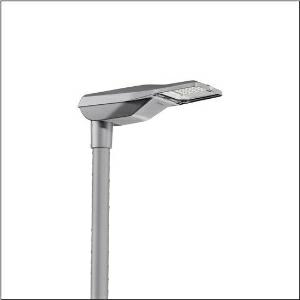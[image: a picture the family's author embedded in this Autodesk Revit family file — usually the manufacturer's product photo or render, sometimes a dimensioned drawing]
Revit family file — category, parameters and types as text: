
# Revit family: streetlight_sl_21_iq_micro___st1_5a_5xe1p41d08db_9421
name_source: partatom
category: Lighting Fixtures
units: mm (PartAtom-declared; Revit-internal decimal feet)

## family parameters
Cut with Voids When Loaded = No
Host = Face
Light Source = No
Part Type = Normal
Room Calculation Point = No
Round Connector Dimension = Use Diameter
Shared = No

## types (1)
- --- (1 x LED, 4930 lm, 36.4 W, 4000K)
    Apparent Load = 36 VA
    CIE Flux Codes = 22 53 95 100 100
    Color Rendering = 70
    Color Temperature = 4000K
    Default Elevation = 1800 mm
    Description = Streetlight SL 21 iQ micro, mast luminaire, primary light control with lens, of PMMA, primary optical cover: cover, of toughened safety glass, transparent, light distribution: ST1.5a, light emission: direct distribution, primary light characteristic: asymmetric, installation type: post-top, side-entry, LED, High Power LED, rated luminous flux: 4.930lm, luminous efficacy: 135lm/W, light colour: 740, colour temperature: 4000K, control gear: iQ-Comfort, control: Auto-Match, Temp-Guard, Lumen-Switch, Night-Set, Smart-Wire, Light-Fading, Desk-Remote (wireless, voltage-free reading and setting of iQ features in the workshop via application-optimized NFC function/RFID function), optimised constant luminous flux control (CLO 2.0), pre-setting: linear dimming characteristic, mains connection: 220..240V, AC, 50/60Hz, start of lifetime: 36W, end of service life: 38W, reduction: 16W, luminaire housing, of diecast aluminium, powder-coated, Siteco® metallic grey (DB 702S), corrosivity category C5 mid according to DIN EN ISO 12944, please order mast flange separately, inclination adjustable: 0°, 5°, 10°, 15°, sealing non-destructively replaceable, multi-level sealing system, length: 528mm, width: 235mm, height: 110mm, mast flange for spigot size: 42mm (side-entry): 5XC10008XM4, 60/48mm (side-entry/post-top): 5XC10108XM2, 76/60mm (side-entry/post-top): 5XC10108XM1, protection rating (complete): IP66, insulation class (complete): insulation class II (safety insulation), certification: CE, ENEC, ENEC+, VDE, impact resistance: IK10, permissible operating ambient temperature for outdoor applications: -40..+50°C, standard-compliant lighting for roads and squares, packaging unit: 1 piece

Light Distribution: ST1.5a
    Height = 110 mm
    Lamp = 1 x LED
    Lamp Light Flux = 4930 lm
    Lamp Power = 36.4 W
    Lamp count = 1
    Length = 528 mm
    Luminous efficacy = 135 lm/W
    Manufacturer = Siteco
    ModVariant = No
    Model = 5XE1P41D08DB
    Number of Poles = 1
    OnlyDefault = Yes
    Power Factor = 1
    Product Name = Streetlight SL 21 iQ micro | ST1.5a
    Product group = mast luminaire | pylon top
    ProductGroupID = 6100
    Protection Class = Protection class II
    Protection Degree = IP 66
    RLX_Detail_Level = 1
    RLX_Emergency_Light_Flux = 0 lm
    RLX_Emergency_Type = 0
    RLX_Emergency_Type_DB = No
    RlxData = <blob elided: 102373 chars, md5=cf2e6f4f>
    Socket = socket
    Standby Power = 0 W
    System Light Flux = 4930 lm
    System Power = 36 W
    Type Comments = factory setting: luminous flux: 100 % | dim-lin: 254 | 715 mA
    Type Image = l_1006881.jpg
    URL = http://relux.com
    VarID = @adj_153864
    Voltage = 0 V
    Weight = 0.00 kg
    Width = 235 mm

## geometry (parser evidence)
native form markers: Blend x4, Sweep x12
no freeform markers — native parametric forms only
